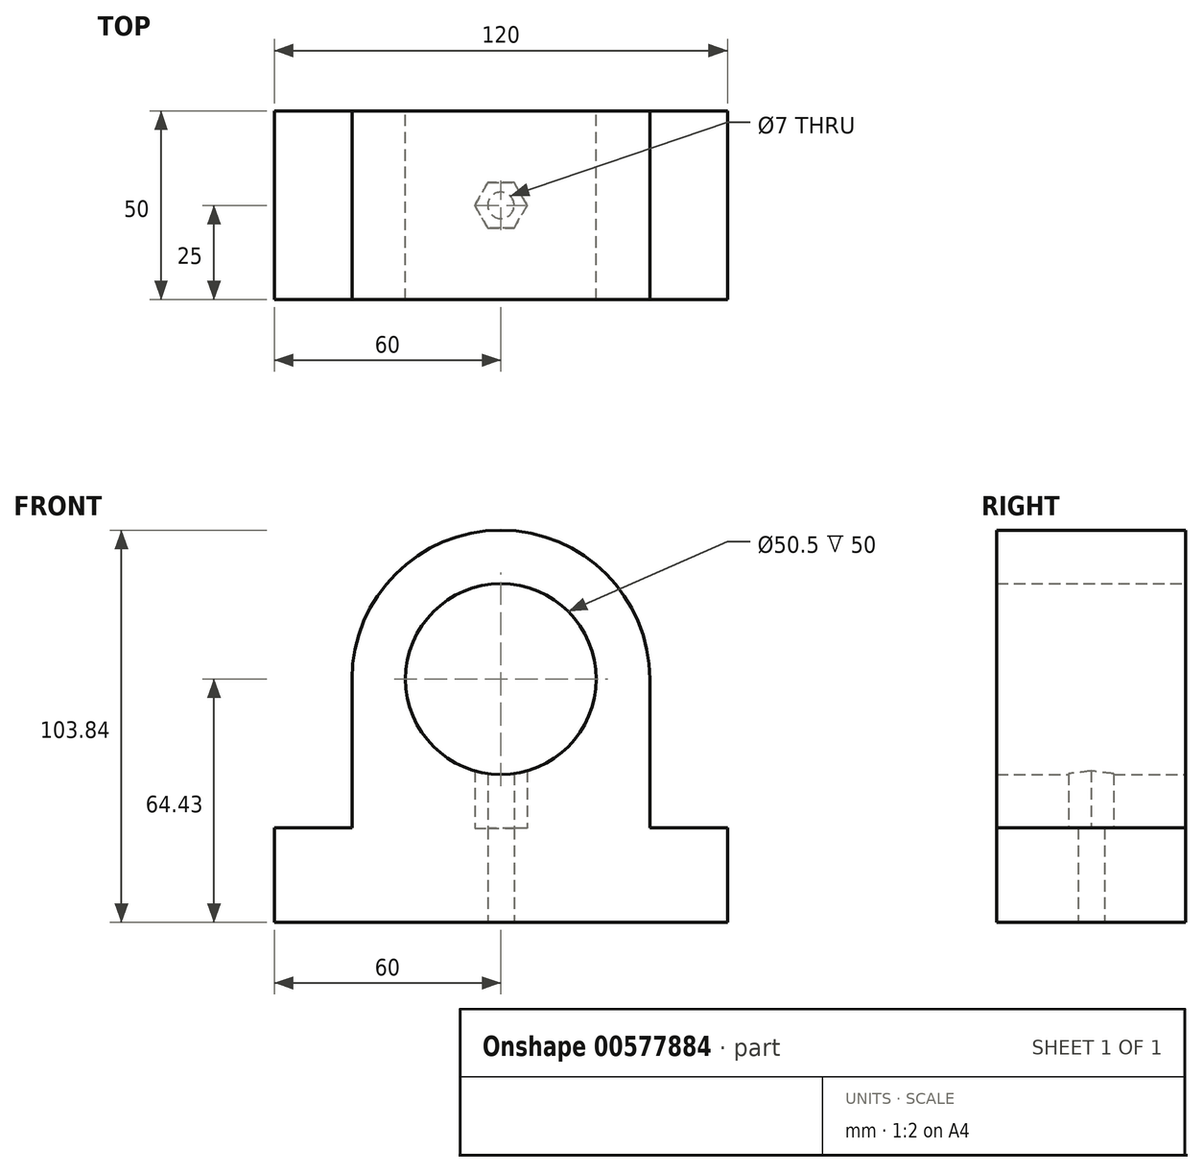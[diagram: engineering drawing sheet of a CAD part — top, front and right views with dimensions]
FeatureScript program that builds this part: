
annotation { "Feature Type Name" : "Feature", "Feature Type Description" : "" }
export const myFeature = defineFeature(function(context is Context, id is Id, definition is map)
    precondition{}
    {
        {
            var Q0;
            Q0=qCreatedBy(makeId("Front.planeOp"),FACE);
            var sketch = newSketch(context, id + "F0", { "sketchPlane" : qUnion([Q0])});
            skCircle(sketch, "E0", {"center": v(0, 0) * mm, "radius": 25.25 * mm});
            skCircle(sketch, "E1", {"center": v(0, 0) * mm, "radius": 39.4 * mm});
            skLineSegment(sketch, "E2.bottom", {"start": v(0, -39.4) * mm, "end": v(60, -39.4) * mm});
            skLineSegment(sketch, "E2.top", {"start": v(0, -64.43) * mm, "end": v(60, -64.43) * mm});
            skLineSegment(sketch, "E2.left", {"start": v(0, -39.4) * mm, "end": v(0, -64.43) * mm});
            skLineSegment(sketch, "E2.right", {"start": v(60, -39.4) * mm, "end": v(60, -64.43) * mm});
            skLineSegment(sketch, "E3.MirrorCS", {"start": v(0, -39.4) * mm, "end": v(-60, -39.4) * mm});
            skLineSegment(sketch, "E4.MirrorCS", {"start": v(0, -64.43) * mm, "end": v(-60, -64.43) * mm});
            skLineSegment(sketch, "E5.MirrorCS", {"start": v(-60, -39.4) * mm, "end": v(-60, -64.43) * mm});
            skLineSegment(sketch, "E6", {"start": v(-39.4, 0) * mm, "end": v(-39.4, -39.4) * mm});
            skLineSegment(sketch, "E7.MirrorCS", {"start": v(39.4, 0) * mm, "end": v(39.4, -39.4) * mm});
            skSolve(sketch);
        }
        {
            var Q0;
            Q0=makeQuery(id+"F0.imprint","IMPRINT",FACE,{"disambiguationData":[TD([[makeQuery(id+"F0.imprint","IMPRINT",EDGE,{"derivedFrom":sQuery(id+"F0.wireOp",EDGE,"E0")}),-1.0]])]});
            var Q1;
            {var subQ3=sQuery(id+"F0.wireOp",EDGE,"E6");Q1=makeQuery(id+"F0.imprint","IMPRINT",FACE,{"disambiguationData":[TD([[makeQuery(id+"F0.imprint","IMPRINT",EDGE,{"derivedFrom":subQ3}),1.0]])]});}
            var Q2;
            {var subQ3=sQuery(id+"F0.wireOp",EDGE,"E2.left");Q2=makeQuery(id+"F0.imprint","IMPRINT",FACE,{"disambiguationData":[TD([[makeQuery(id+"F0.imprint","IMPRINT",EDGE,{"derivedFrom":subQ3}),-1.0]])]});}
            var Q3;
            Q3=makeQuery(id+"F0.imprint","IMPRINT",FACE,{"disambiguationData":[TD([[makeQuery(id+"F0.imprint","IMPRINT",EDGE,{"derivedFrom":sQuery(id+"F0.wireOp",EDGE,"E2.top")}),1.0]])]});
            var Q4;
            {var subQ3=sQuery(id+"F0.wireOp",EDGE,"E7.MirrorCS");Q4=makeQuery(id+"F0.imprint","IMPRINT",FACE,{"disambiguationData":[TD([[makeQuery(id+"F0.imprint","IMPRINT",EDGE,{"derivedFrom":subQ3}),-1.0]])]});}
            extrude(context, id + "F1", {"entities" : qUnion([Q0, Q1, Q2, Q3, Q4]), "depth" : 50 * mm, "offsetDistance" : 25 * mm});
        }
        {
            var Q0;
            Q0=makeQuery(id+"F1.opExtrude","SWEPT_FACE",FACE,{"disambiguationData":[OSD([sQuery(id+"F0.wireOp",EDGE,"E2.top"),sQuery(id+"F0.wireOp",EDGE,"E4.MirrorCS")])]});
            cPlane(context, id + "F2", {"entities" : qUnion([Q0]), "cplaneType" : CPlaneType.OFFSET, "offset" : 25 * mm, "oppositeDirection" : true, "width" : 150 * mm, "height" : 150 * mm});
        }
        {
            var Q0;
            Q0=makeQuery(id+"F1.opExtrude","SWEPT_FACE",FACE,{"disambiguationData":[OSD([sQuery(id+"F0.wireOp",EDGE,"E2.top"),sQuery(id+"F0.wireOp",EDGE,"E4.MirrorCS")])]});
            var sketch = newSketch(context, id + "F3", { "sketchPlane" : qUnion([Q0])});
            skLineSegment(sketch, "E8", {"start": v(-60, 25) * mm, "end": v(60, 25) * mm});
            skCircle(sketch, "E9", {"center": v(0, 25) * mm, "radius": 6.25 * mm});
            skSolve(sketch);
        }
        {
            var Q0;
            Q0=sQuery(id+"F3.wireOp",VERTEX,"E9.center");
            var Q1;
            Q1=makeQuery(id+"F1.opExtrude","SWEPT_BODY",BODY,{"disambiguationData":[OSD([sQuery(id+"F0.wireOp",EDGE,"E0"),sQuery(id+"F0.wireOp",EDGE,"E1"),sQuery(id+"F0.wireOp",EDGE,"E2.bottom"),sQuery(id+"F0.wireOp",EDGE,"E2.top"),sQuery(id+"F0.wireOp",EDGE,"E2.right"),sQuery(id+"F0.wireOp",EDGE,"E3.MirrorCS"),sQuery(id+"F0.wireOp",EDGE,"E4.MirrorCS"),sQuery(id+"F0.wireOp",EDGE,"E5.MirrorCS"),sQuery(id+"F0.wireOp",EDGE,"E6"),sQuery(id+"F0.wireOp",EDGE,"E7.MirrorCS")])]});
            hole(context, id + "F4", {"style" : HoleStyle.SIMPLE, "endStyle" : HoleEndStyle.BLIND, "holeDiameter" : 7 * mm, "holeDepth" : 70 * mm, "isTappedThrough" : true, "tappedDepth" : 12 * mm, "tapClearance" : 3, "locations" : qUnion([Q0]), "scope" : qUnion([Q1])});
        }
        {
            var Q0;
            Q0=qCreatedBy(id+"F2.planeOp",FACE);
            var sketch = newSketch(context, id + "F5", { "sketchPlane" : qUnion([Q0])});
            skCircle(sketch, "E10.cCircle", {"center": v(0, 25) * mm, "radius": 6.02 * mm, "construction": true});
            skLineSegment(sketch, "E10.0", {"start": v(3.47, 18.98) * mm, "end": v(-3.47, 18.98) * mm});
            skLineSegment(sketch, "E10.1", {"start": v(-3.47, 18.98) * mm, "end": v(-6.95, 25) * mm});
            skLineSegment(sketch, "E10.2", {"start": v(-6.95, 25) * mm, "end": v(-3.47, 31.02) * mm});
            skLineSegment(sketch, "E10.3", {"start": v(-3.47, 31.02) * mm, "end": v(3.47, 31.02) * mm});
            skLineSegment(sketch, "E10.4", {"start": v(3.47, 31.02) * mm, "end": v(6.95, 25) * mm});
            skLineSegment(sketch, "E10.5", {"start": v(6.95, 25) * mm, "end": v(3.47, 18.98) * mm});
            skPoint(sketch, "E10.0.midPoint", {"position": v(0, 18.98) * mm});
            skSolve(sketch);
        }
        {
            var Q0;
            Q0 = qSketchRegion(id + "F5", true);
            extrude(context, id + "F6", {"entities" : qUnion([Q0]), "operationType" : NewBodyOperationType.REMOVE, "oppositeDirection" : true, "depth" : 25 * mm, "offsetDistance" : 25 * mm});
        }
    });
